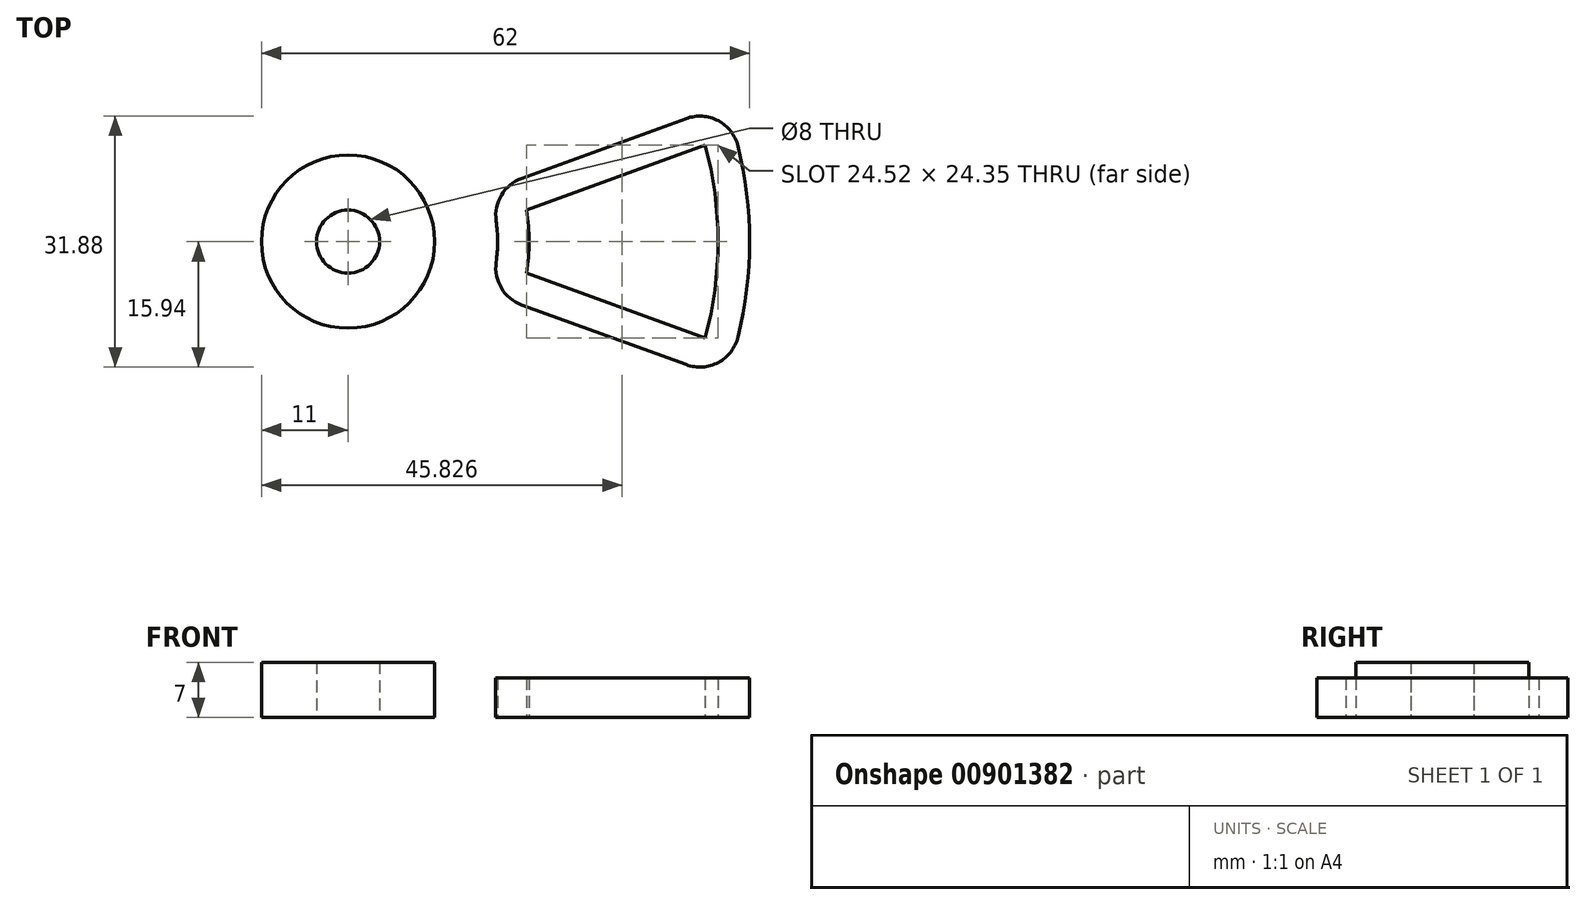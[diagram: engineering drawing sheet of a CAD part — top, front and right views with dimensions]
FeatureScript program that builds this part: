
annotation { "Feature Type Name" : "Feature", "Feature Type Description" : "" }
export const myFeature = defineFeature(function(context is Context, id is Id, definition is map)
    precondition{}
    {
        {
            var Q0;
            Q0=qCreatedBy(makeId("Top.planeOp"),FACE);
            var sketch = newSketch(context, id + "F0", { "sketchPlane" : qUnion([Q0])});
            skLineSegment(sketch, "E0", {"start": v(22.06, 8.03) * mm, "end": v(42.97, 15.64) * mm});
            skLineSegment(sketch, "E1.MirrorCS", {"start": v(22.06, -8.03) * mm, "end": v(42.97, -15.64) * mm});
            skArc(sketch, "E2", {"start": v(49.54, -12.13) * mm, "mid": v(51, 0) * mm, "end": v(49.54, 12.13) * mm});
            skArc(sketch, "E3", {"start": v(18.82, -2.64) * mm, "mid": v(19, 0) * mm, "end": v(18.82, 2.64) * mm});
            skPoint(sketch, "E4.visualSharp", {"position": v(17.85, 6.5) * mm});
            skArc(sketch, "E4.filletArc", {"start": v(22.06, 8.03) * mm, "mid": v(19.48, 5.9) * mm, "end": v(18.82, 2.64) * mm});
            skPoint(sketch, "E5.visualSharp", {"position": v(17.85, -6.5) * mm});
            skArc(sketch, "E5.filletArc", {"start": v(18.82, -2.64) * mm, "mid": v(19.48, -5.9) * mm, "end": v(22.06, -8.03) * mm});
            skPoint(sketch, "E6.visualSharp", {"position": v(47.92, -17.44) * mm});
            skArc(sketch, "E6.filletArc", {"start": v(42.97, -15.64) * mm, "mid": v(47.04, -15.35) * mm, "end": v(49.54, -12.13) * mm});
            skPoint(sketch, "E7.visualSharp", {"position": v(47.92, 17.44) * mm});
            skArc(sketch, "E7.filletArc", {"start": v(49.54, 12.13) * mm, "mid": v(47.04, 15.35) * mm, "end": v(42.97, 15.64) * mm});
            skLineSegment(sketch, "E8.0", {"start": v(22.65, 3.99) * mm, "end": v(45.37, 12.26) * mm});
            skArc(sketch, "E8.1", {"start": v(22.65, -3.99) * mm, "mid": v(23, 0) * mm, "end": v(22.65, 3.99) * mm});
            skLineSegment(sketch, "E8.2", {"start": v(22.65, -3.99) * mm, "end": v(45.37, -12.26) * mm});
            skArc(sketch, "E8.3", {"start": v(45.37, -12.26) * mm, "mid": v(47, 0) * mm, "end": v(45.37, 12.26) * mm});
            skSolve(sketch);
        }
        {
            var Q0;
            Q0=makeQuery(id+"F0.imprint","IMPRINT",FACE,{"disambiguationData":[TD([[makeQuery(id+"F0.imprint","IMPRINT",EDGE,{"derivedFrom":sQuery(id+"F0.wireOp",EDGE,"E0")}),-1.0]])]});
            extrude(context, id + "F1", {"entities" : qUnion([Q0]), "depth" : 5 * mm, "offsetDistance" : 25 * mm});
        }
        {
            var Q0;
            Q0=qCreatedBy(makeId("Top.planeOp"),FACE);
            var sketch = newSketch(context, id + "F2", { "sketchPlane" : qUnion([Q0])});
            skCircle(sketch, "E9", {"center": v(0, 0) * mm, "radius": 11 * mm});
            skCircle(sketch, "E10", {"center": v(0, 0) * mm, "radius": 4 * mm});
            skSolve(sketch);
        }
        {
            var Q0;
            Q0=makeQuery(id+"F2.imprint","IMPRINT",FACE,{"disambiguationData":[TD([[makeQuery(id+"F2.imprint","IMPRINT",EDGE,{"derivedFrom":sQuery(id+"F2.wireOp",EDGE,"E9")}),1.0]])]});
            extrude(context, id + "F3", {"entities" : qUnion([Q0]), "depth" : 7 * mm, "offsetDistance" : 25 * mm});
        }
    });
